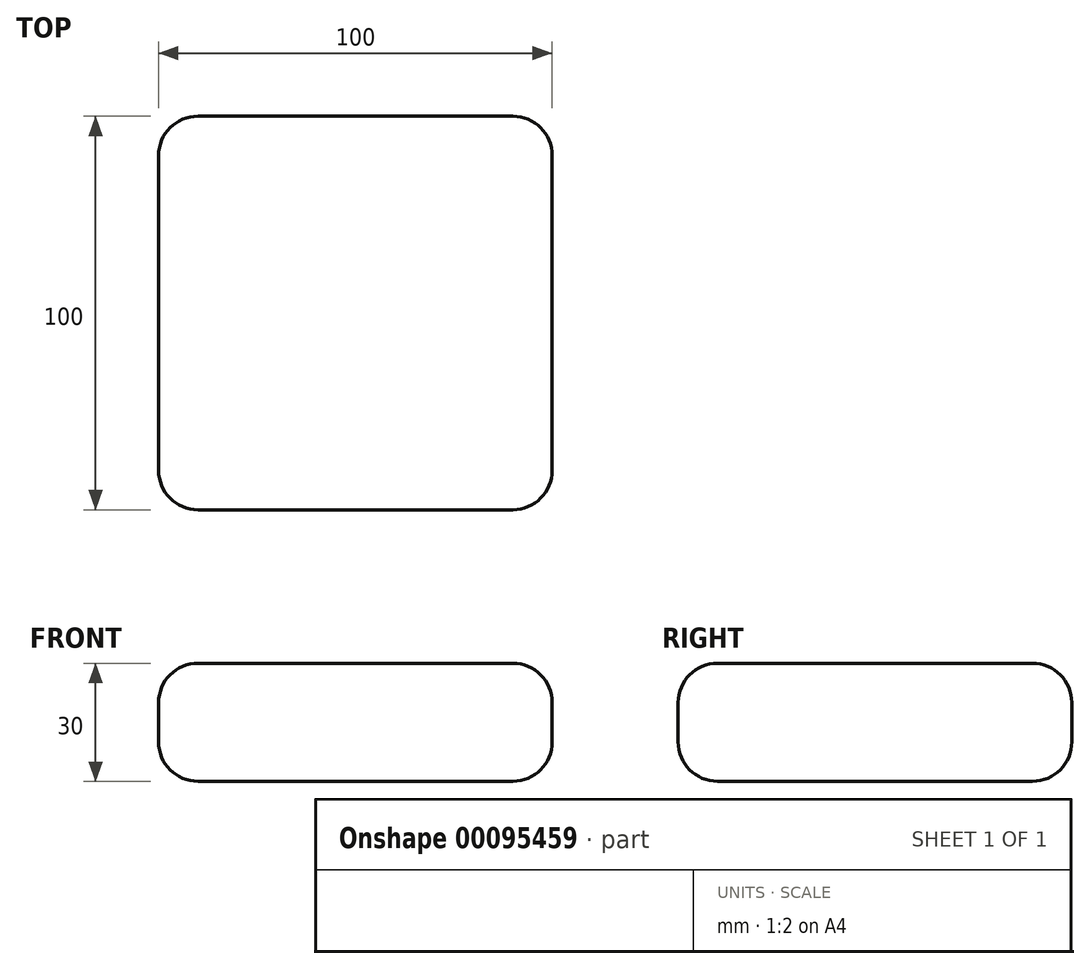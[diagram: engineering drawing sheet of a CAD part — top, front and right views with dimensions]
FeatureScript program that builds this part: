
annotation { "Feature Type Name" : "Feature", "Feature Type Description" : "" }
export const myFeature = defineFeature(function(context is Context, id is Id, definition is map)
    precondition{}
    {
        {
            var Q0;
            Q0=qCreatedBy(makeId("Top.planeOp"),FACE);
            var sketch = newSketch(context, id + "F0", { "sketchPlane" : qUnion([Q0])});
            skLineSegment(sketch, "E0.bottom", {"start": v(50, -50) * mm, "end": v(-50, -50) * mm});
            skLineSegment(sketch, "E0.top", {"start": v(50, 50) * mm, "end": v(-50, 50) * mm});
            skLineSegment(sketch, "E0.left", {"start": v(50, -50) * mm, "end": v(50, 50) * mm});
            skLineSegment(sketch, "E0.right", {"start": v(-50, -50) * mm, "end": v(-50, 50) * mm});
            skPoint(sketch, "E0.middle", {"position": v(0, 0) * mm});
            skSolve(sketch);
        }
        {
            var Q0;
            Q0 = qSketchRegion(id + "F0", true);
            extrude(context, id + "F1", {"entities" : qUnion([Q0]), "depth" : 30 * mm});
        }
        {
            var Q0;
            Q0=makeQuery(id+"F1.opExtrude","SWEPT_FACE",FACE,{"disambiguationData":[OSD([sQuery(id+"F0.wireOp",EDGE,"E0.bottom")])]});
            var Q1;
            Q1=makeQuery(id+"F1.opExtrude","CAP_FACE",FACE,{"disambiguationData":[OSD([sQuery(id+"F0.wireOp",EDGE,"E0.bottom"),sQuery(id+"F0.wireOp",EDGE,"E0.top"),sQuery(id+"F0.wireOp",EDGE,"E0.left"),sQuery(id+"F0.wireOp",EDGE,"E0.right")])],"isStart":false});
            var Q2;
            Q2=makeQuery(id+"F1.opExtrude","SWEPT_FACE",FACE,{"disambiguationData":[OSD([sQuery(id+"F0.wireOp",EDGE,"E0.left")])]});
            var Q3;
            Q3=makeQuery(id+"F1.opExtrude","SWEPT_FACE",FACE,{"disambiguationData":[OSD([sQuery(id+"F0.wireOp",EDGE,"E0.right")])]});
            var Q4;
            Q4=makeQuery(id+"F1.opExtrude","SWEPT_FACE",FACE,{"disambiguationData":[OSD([sQuery(id+"F0.wireOp",EDGE,"E0.top")])]});
            var Q5;
            Q5=makeQuery(id+"F1.opExtrude","CAP_FACE",FACE,{"disambiguationData":[OSD([sQuery(id+"F0.wireOp",EDGE,"E0.bottom"),sQuery(id+"F0.wireOp",EDGE,"E0.top"),sQuery(id+"F0.wireOp",EDGE,"E0.left"),sQuery(id+"F0.wireOp",EDGE,"E0.right")])],"isStart":true});
            fillet(context, id + "F2", {"entities" : qUnion([Q0, Q1, Q2, Q3, Q4, Q5]), "radius" : 10 * mm, "tangentPropagation" : true, "allowEdgeOverflow" : false});
        }
    });
